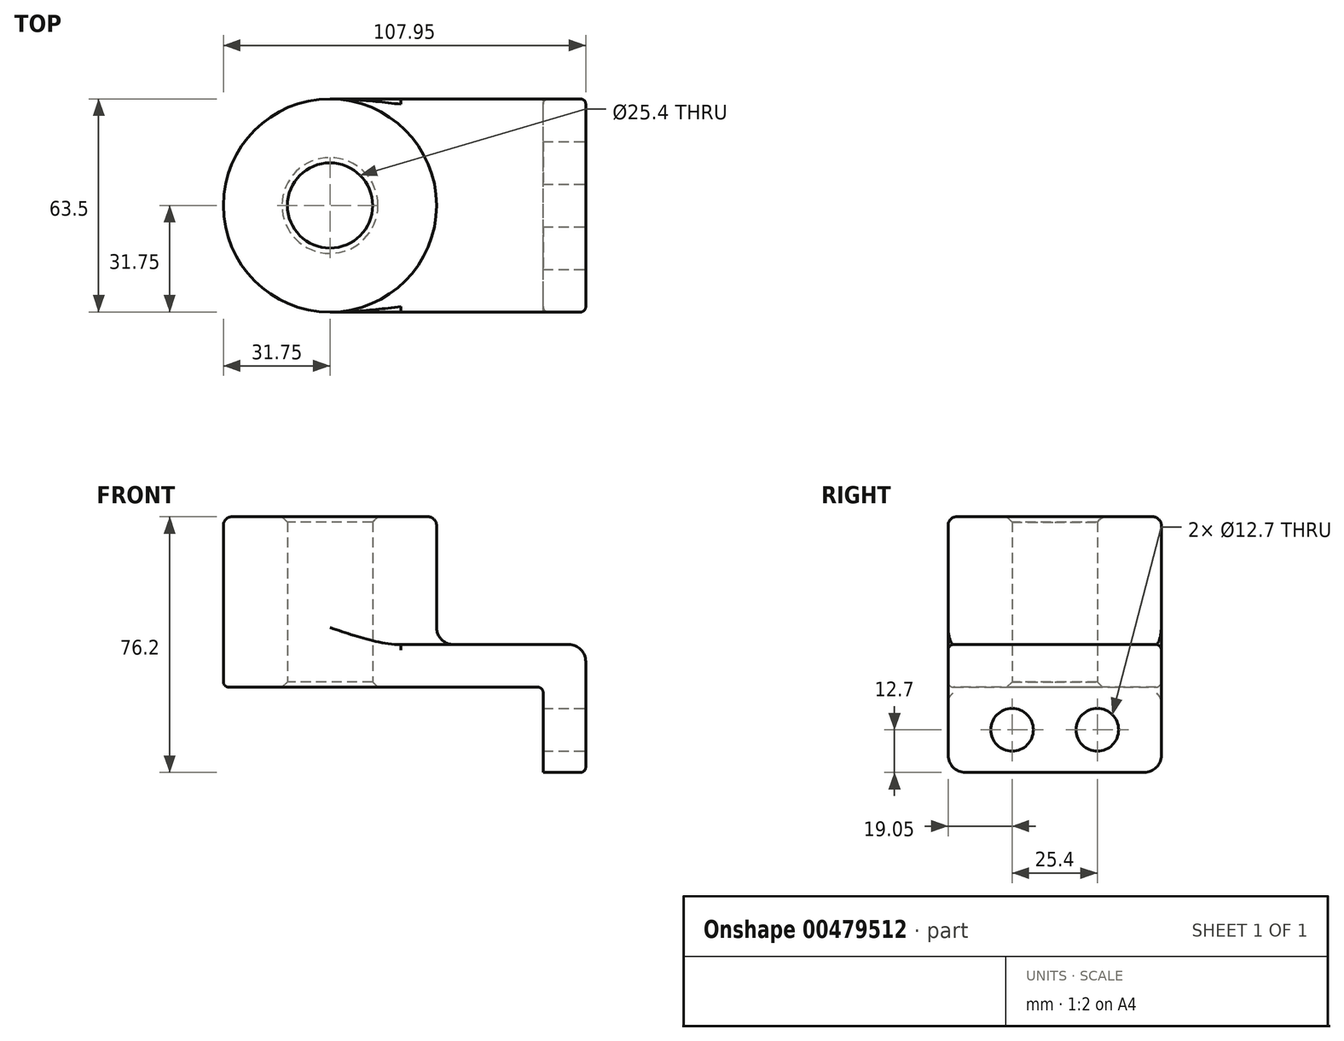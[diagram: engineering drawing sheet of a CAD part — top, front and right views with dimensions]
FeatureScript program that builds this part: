
annotation { "Feature Type Name" : "Feature", "Feature Type Description" : "" }
export const myFeature = defineFeature(function(context is Context, id is Id, definition is map)
    precondition{}
    {
        {
            var Q0;
            Q0=qCreatedBy(makeId("Top.planeOp"),FACE);
            var sketch = newSketch(context, id + "F0", { "sketchPlane" : qUnion([Q0])});
            skLineSegment(sketch, "E0.bottom", {"start": v(-38.1, 31.75) * mm, "end": v(38.1, 31.75) * mm});
            skLineSegment(sketch, "E0.top", {"start": v(-38.1, -31.75) * mm, "end": v(38.1, -31.75) * mm});
            skLineSegment(sketch, "E0.left", {"start": v(-38.1, 31.75) * mm, "end": v(-38.1, -31.75) * mm});
            skLineSegment(sketch, "E0.right", {"start": v(38.1, 31.75) * mm, "end": v(38.1, -31.75) * mm});
            skPoint(sketch, "E0.middle", {"position": v(0, 0) * mm});
            skCircle(sketch, "E1", {"center": v(-38.1, 0) * mm, "radius": 31.75 * mm});
            skCircle(sketch, "E2", {"center": v(-38.1, 0) * mm, "radius": 12.7 * mm});
            skSolve(sketch);
        }
        {
            var Q0;
            Q0 = qSketchRegion(id + "F0", true);
            extrude(context, id + "F1", {"entities" : qUnion([Q0]), "depth" : 12.7 * mm});
        }
        {
            var Q0;
            {var subQ1=sQuery(id+"F0.wireOp",EDGE,"E0.left");var subQ3=sQuery(id+"F0.wireOp",EDGE,"E2");var subQ4=makeQuery(id+"F0.imprint","INTERSECT",VERTEX,{"disambiguationData":[OD(0.0)],"derivedFrom":[subQ1,subQ3]});Q0=makeQuery(id+"F0.imprint","IMPRINT",FACE,{"disambiguationData":[TD([[makeQuery(id+"F0.imprint","IMPRINT",EDGE,{"disambiguationData":[TD([[subQ4,1.0]])],"derivedFrom":subQ3}),-1.0]])]});}
            var Q1;
            {var subQ1=sQuery(id+"F0.wireOp",EDGE,"E0.left");var subQ3=sQuery(id+"F0.wireOp",EDGE,"E2");var subQ4=makeQuery(id+"F0.imprint","INTERSECT",VERTEX,{"disambiguationData":[OD(0.0)],"derivedFrom":[subQ1,subQ3]});Q1=makeQuery(id+"F0.imprint","IMPRINT",FACE,{"disambiguationData":[TD([[makeQuery(id+"F0.imprint","IMPRINT",EDGE,{"disambiguationData":[TD([[subQ4,-1.0]])],"derivedFrom":subQ3}),-1.0]])]});}
            extrude(context, id + "F2", {"entities" : qUnion([Q0, Q1]), "operationType" : NewBodyOperationType.ADD, "depth" : 50.8 * mm});
        }
        {
            var Q0;
            Q0=makeQuery(id+"F1.opExtrude","SWEPT_FACE",FACE,{"disambiguationData":[OSD([sQuery(id+"F0.wireOp",EDGE,"E0.right")])]});
            var sketch = newSketch(context, id + "F3", { "sketchPlane" : qUnion([Q0])});
            skLineSegment(sketch, "E3.bottom", {"start": v(-31.75, 12.7) * mm, "end": v(31.75, 12.7) * mm});
            skLineSegment(sketch, "E3.top", {"start": v(-31.75, -25.4) * mm, "end": v(31.75, -25.4) * mm});
            skLineSegment(sketch, "E3.left", {"start": v(-31.75, 12.7) * mm, "end": v(-31.75, -25.4) * mm});
            skLineSegment(sketch, "E3.right", {"start": v(31.75, 12.7) * mm, "end": v(31.75, -25.4) * mm});
            skCircle(sketch, "E4", {"center": v(-12.7, -12.7) * mm, "radius": 6.35 * mm});
            skLineSegment(sketch, "E5", {"start": v(0, 0) * mm, "end": v(0, -25.4) * mm, "construction": true});
            skCircle(sketch, "E6.MirrorC", {"center": v(12.7, -12.7) * mm, "radius": 6.35 * mm});
            skSolve(sketch);
        }
        {
            var Q0;
            Q0 = qSketchRegion(id + "F3", true);
            extrude(context, id + "F4", {"entities" : qUnion([Q0]), "operationType" : NewBodyOperationType.ADD, "oppositeDirection" : true, "depth" : 12.7 * mm});
        }
        {
            var Q0;
            {var subQ0=sQuery(id+"F0.wireOp",EDGE,"E1");Q0=makeQuery(id+"F2.boolean.opBoolean","INTERSECT",EDGE,{"derivedFrom":[makeQuery(id+"F1.opExtrude","CAP_FACE",FACE,{"disambiguationData":[OSD([sQuery(id+"F0.wireOp",EDGE,"E0.bottom"),sQuery(id+"F0.wireOp",EDGE,"E0.top"),sQuery(id+"F0.wireOp",EDGE,"E0.right"),subQ0,sQuery(id+"F0.wireOp",EDGE,"E2")])],"isStart":false}),makeQuery(id+"F2.opExtrude","SWEPT_FACE",FACE,{"disambiguationData":[OSD([subQ0])]})]});}
            var Q1;
            Q1=makeQuery(id+"F1.opExtrude","CAP_EDGE",EDGE,{"disambiguationData":[OSD([sQuery(id+"F0.wireOp",EDGE,"E0.right")])],"isStart":false});
            var Q2;
            Q2=makeQuery(id+"F4.opExtrude","SWEPT_EDGE",EDGE,{"disambiguationData":[OSD([sQuery(id+"F3.wireOp",EDGE,"E3.top"),sQuery(id+"F3.wireOp",EDGE,"E3.left")])]});
            var Q3;
            Q3=makeQuery(id+"F4.opExtrude","SWEPT_EDGE",EDGE,{"disambiguationData":[OSD([sQuery(id+"F3.wireOp",EDGE,"E3.top"),sQuery(id+"F3.wireOp",EDGE,"E3.right")])]});
            fillet(context, id + "F5", {"entities" : qUnion([Q0, Q1, Q2, Q3]), "radius" : 5.08 * mm, "tangentPropagation" : true, "allowEdgeOverflow" : false});
        }
        {
            var Q0;
            Q0=makeQuery(id+"F1.opExtrude","CAP_EDGE",EDGE,{"disambiguationData":[OSD([sQuery(id+"F0.wireOp",EDGE,"E0.top")])],"isStart":false});
            var Q1;
            Q1=makeQuery(id+"F1.opExtrude","CAP_EDGE",EDGE,{"disambiguationData":[OSD([sQuery(id+"F0.wireOp",EDGE,"E0.top")])],"isStart":true});
            var Q2;
            Q2=makeQuery(id+"F4.boolean.opBoolean","INTERSECT",EDGE,{"derivedFrom":[makeQuery(id+"F1.opExtrude","CAP_FACE",FACE,{"disambiguationData":[OSD([sQuery(id+"F0.wireOp",EDGE,"E0.bottom"),sQuery(id+"F0.wireOp",EDGE,"E0.top"),sQuery(id+"F0.wireOp",EDGE,"E0.right"),sQuery(id+"F0.wireOp",EDGE,"E1"),sQuery(id+"F0.wireOp",EDGE,"E2")])],"isStart":true}),makeQuery(id+"F4.opExtrude","CAP_FACE",FACE,{"disambiguationData":[OSD([sQuery(id+"F3.wireOp",EDGE,"E3.bottom"),sQuery(id+"F3.wireOp",EDGE,"E3.top"),sQuery(id+"F3.wireOp",EDGE,"E3.left"),sQuery(id+"F3.wireOp",EDGE,"E3.right"),sQuery(id+"F3.wireOp",EDGE,"E4"),sQuery(id+"F3.wireOp",EDGE,"E6.MirrorC")])],"isStart":false})]});
            fillet(context, id + "F6", {"entities" : qUnion([Q0, Q1, Q2]), "radius" : 1.59 * mm, "tangentPropagation" : true, "allowEdgeOverflow" : false});
        }
        {
            var Q0;
            {var subQ0=sQuery(id+"F0.wireOp",EDGE,"E2");Q0=makeQuery(id+"F2.boolean.opBoolean","MERGE",FACE,{"derivedFrom":[makeQuery(id+"F1.opExtrude","SWEPT_FACE",FACE,{"disambiguationData":[OSD([subQ0])]}),makeQuery(id+"F2.opExtrude","SWEPT_FACE",FACE,{"disambiguationData":[OSD([subQ0])]})]});}
            chamfer(context, id + "F7", {"entities" : qUnion([Q0]), "width" : 1.59 * mm, "tangentPropagation" : true});
        }
        {
            var Q0;
            Q0=makeQuery(id+"F2.opExtrude","CAP_FACE",FACE,{"disambiguationData":[OSD([sQuery(id+"F0.wireOp",EDGE,"E1"),sQuery(id+"F0.wireOp",EDGE,"E2")])],"isStart":false});
            fillet(context, id + "F8", {"entities" : qUnion([Q0]), "radius" : 2.54 * mm, "tangentPropagation" : true, "allowEdgeOverflow" : false});
        }
    });
